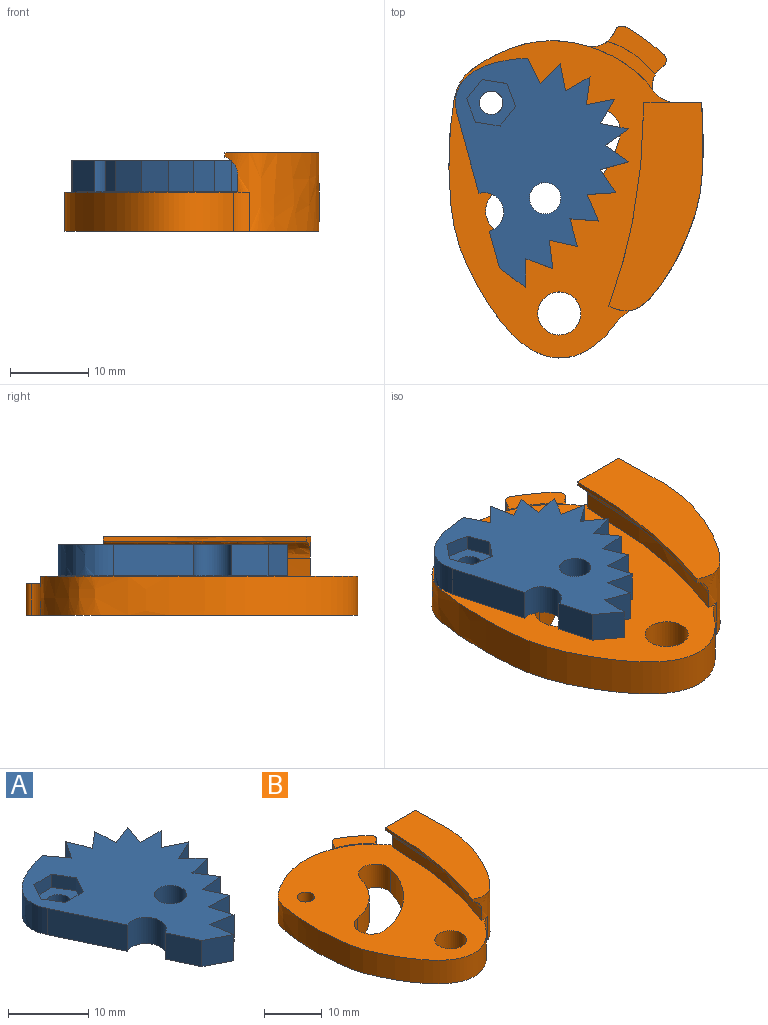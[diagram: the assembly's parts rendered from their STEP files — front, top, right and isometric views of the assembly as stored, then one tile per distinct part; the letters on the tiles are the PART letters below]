
ASSEMBLY  parts=2 mates=1
PART A: 36 faces, bbox 23.7x28.9x4 mm
  f0: cylinder r=1.5mm len=3mm, axis (0,0,-1), area 18.8mm2, adj f28,f35
  f1: cylinder r=2.5mm len=4.76mm, axis (0,0,-1), area 31.4mm2, adj f2,f26,f27,f28
  f2: plane 4.41x4mm, normal (-0.9,-0.43,0), area 19.5mm2, adj f1,f3,f27,f28
  f3: plane 4x3.67mm, normal (-0.45,-0.89,0), area 16.5mm2, adj f2,f4,f27,f28
  f4: plane 4x3.6mm, normal (0.99,0.15,0), area 14.6mm2, adj f3,f5,f27,f28
  f5: plane 4x3.6mm, normal (-0.18,-0.98,0), area 14.6mm2, adj f4,f6,f27,f28
  f6: plane 4x3.49mm, normal (0.96,0.29,0), area 14.6mm2, adj f5,f7,f27,f28
  f7: plane 4x3.66mm, normal (-0.04,-1,0), area 14.7mm2, adj f6,f8,f27,f28
  f8: plane 4x3.31mm, normal (0.91,0.42,0), area 14.6mm2, adj f7,f9,f27,f28
  f9: plane 4x3.62mm, normal (0.1,-1,0), area 14.6mm2, adj f8,f10,f27,f28
  f10: plane 4x3.08mm, normal (0.84,0.55,0), area 14.7mm2, adj f9,f11,f27,f28
  f11: plane 4x3.56mm, normal (0.24,-0.97,0), area 14.7mm2, adj f10,f12,f27,f28
  f12: plane 4x2.56mm, normal (0.72,0.7,0), area 14.3mm2, adj f11,f13,f27,f28
  f13: plane 4x3.37mm, normal (0.43,-0.9,0), area 14.9mm2, adj f12,f14,f27,f28
  f14: plane 4x3.27mm, normal (0.43,0.9,0), area 14.5mm2, adj f13,f15,f27,f28
  f15: plane 4x2.59mm, normal (0.71,-0.7,0), area 14.5mm2, adj f14,f16,f27,f28
  f16: plane 4x3.62mm, normal (0.02,1,0), area 14.5mm2, adj f15,f17,f27,f28
  f17: plane 4x3.38mm, normal (0.94,-0.34,0), area 14.4mm2, adj f16,f18,f27,f28
  f18: plane 4x3.4mm, normal (-0.36,0.93,0), area 14.6mm2, adj f17,f19,f27,f28
  f19: plane 4x3.58mm, normal (1,0.04,0), area 14.3mm2, adj f18,f20,f27,f28
  f20: plane 4x2.79mm, normal (-0.64,0.77,0), area 14.5mm2, adj f19,f21,f27,f28
  f21: plane 4x3.38mm, normal (0.93,0.36,0), area 14.5mm2, adj f20,f22,f27,f28
  f22: plane 4x3.03mm, normal (-0.83,0.55,0), area 14.6mm2, adj f21,f23,f27,f28
  f23: plane 4x2.93mm, normal (0.8,0.6,0), area 14.6mm2, adj f22,f24,f27,f28
  f24: extruded ~8.5x8.16mm, area 53.4mm2, adj f23,f26,f27,f28
  f25: cylinder r=2mm len=4mm, axis (0,0,-1), area 50.3mm2, adj f27,f28
  f26: plane 9.57x4.53mm, normal (-0.9,-0.43,0), area 42.4mm2, adj f1,f24,f27,f28
  f27: plane 28.95x23.7mm, normal (0,0,1), area 337.2mm2, adj f1,f2,f3,f4,f5,f6,f7,f8
  f28: plane 28.95x23.7mm, normal (0,0,-1), area 356.3mm2, adj f0,f1,f2,f3,f4,f5,f6,f7
  f29: plane 3.18x2mm, normal (-0.02,1,0), area 6.4mm2, adj f27,f30,f34,f35
  f30: plane 2.78x2mm, normal (-0.87,0.49,0), area 6.4mm2, adj f27,f29,f31,f35
  f31: plane 2.72x2mm, normal (-0.86,-0.51,0), area 6.4mm2, adj f27,f30,f32,f35
  f32: plane 3.18x2mm, normal (0.02,-1,0), area 6.4mm2, adj f27,f31,f33,f35
  f33: plane 2.78x2mm, normal (0.87,-0.49,0), area 6.4mm2, adj f27,f32,f34,f35
  f34: plane 2.72x2mm, normal (0.86,0.51,0), area 6.4mm2, adj f27,f29,f33,f35
  f35: plane 6.35x5.55mm, normal (0,0,1), area 19.1mm2, adj f0,f29,f30,f31,f32,f33,f34
PART B: 26 faces, bbox 33.5x43.2x11 mm
  f0: cylinder r=3mm len=5.89mm, axis (0,0,-1), area 47.1mm2, adj f1,f6,f7,f8
  f1: cylinder r=17mm len=13.6mm, axis (0,0,-1), area 96.7mm2, adj f0,f2,f7,f8
  f2: cylinder r=3mm len=5.96mm, axis (0,0,-1), area 47.1mm2, adj f1,f6,f7,f8
  f3: cylinder r=2.75mm len=5.5mm, axis (0,0,-1), area 86.4mm2, adj f7,f8
  f4: cylinder r=1.5mm len=5mm, axis (0,0,-1), area 47.1mm2, adj f7,f8
  f5: extruded ~40.47x25.98mm, area 372.1mm2, adj f7,f8,f13,f14,f18,f24
  f6: cylinder r=11mm len=8.8mm, axis (0,0,-1), area 62.6mm2, adj f0,f2,f7,f8
  f7: plane 41.6x29.95mm, normal (0,0,1), area 703.6mm2, adj f0,f1,f2,f3,f4,f5,f6,f9
  f8: plane 42.67x32.98mm, normal (0,0,-1), area 877.4mm2, adj f0,f1,f2,f3,f4,f5,f6,f9
  f9: extruded ~26.54x12.03mm, area 301.3mm2, adj f7,f8,f10,f11,f12,f13,f15,f16
  f10: plane 10.29x7.69mm, normal (0,1,0), area 45.3mm2, adj f7,f8,f9,f11,f12,f14,f15,f16
  f11: extruded ~25.93x4.45mm, area 14.5mm2, adj f9,f10,f12,f16
  f12: plane 26.84x12.32mm, normal (0,0,1), area 188.8mm2, adj f9,f10,f11
  f13: cylinder r=4mm len=5mm, axis (0,0,-1), area 12.7mm2, adj f5,f7,f8,f9
  f14: cylinder r=4mm len=5mm, axis (0,0,-1), area 19mm2, adj f5,f7,f8,f10,f25
  f15: bspline ~30.26x5.68mm, area 60.8mm2, adj f7,f9,f10,f16
  f16: bspline ~30.26x9.31mm, area 82.3mm2, adj f9,f10,f11,f15
  f17: plane 4x0.22mm, normal (0.6,-0.8,0), area 1.1mm2, adj f8,f20,f23,f25
  f18: plane 8.95x6.32mm, normal (0,0,1), area 12.9mm2, adj f5,f19,f24,f25
  f19: cylinder r=11.55mm len=6.09mm, axis (0,0,-1), area 15.2mm2, adj f18,f23,f24,f25
  f20: cylinder r=1mm len=4mm, axis (0,0,-1), area 7.1mm2, adj f8,f17,f21,f23
  f21: cylinder r=31.28mm len=4.82mm, axis (0,0,-1), area 23.8mm2, adj f8,f20,f22,f23
  f22: cylinder r=1mm len=4mm, axis (0,0,-1), area 7mm2, adj f8,f21,f23,f24
  f23: plane 7.54x6.26mm, normal (0,0,1), area 18.5mm2, adj f17,f19,f20,f21,f22,f24,f25
  f24: cylinder r=3mm len=4mm, axis (0,0,-1), area 12.3mm2, adj f5,f8,f18,f19,f22,f23
  f25: cylinder r=3mm len=4mm, axis (0,0,-1), area 9mm2, adj f8,f14,f17,f18,f19,f23
PLACE A rot(axis=(0,0,-1),10deg) t=(-19.82,-68.35,21.77)mm
PLACE B t=(2.08,-32.11,16.77)mm fixed
MATE revolute A.f0 <-> B.f1  axis (0,0,-1) through (7.7,0.45,21.77)mm
